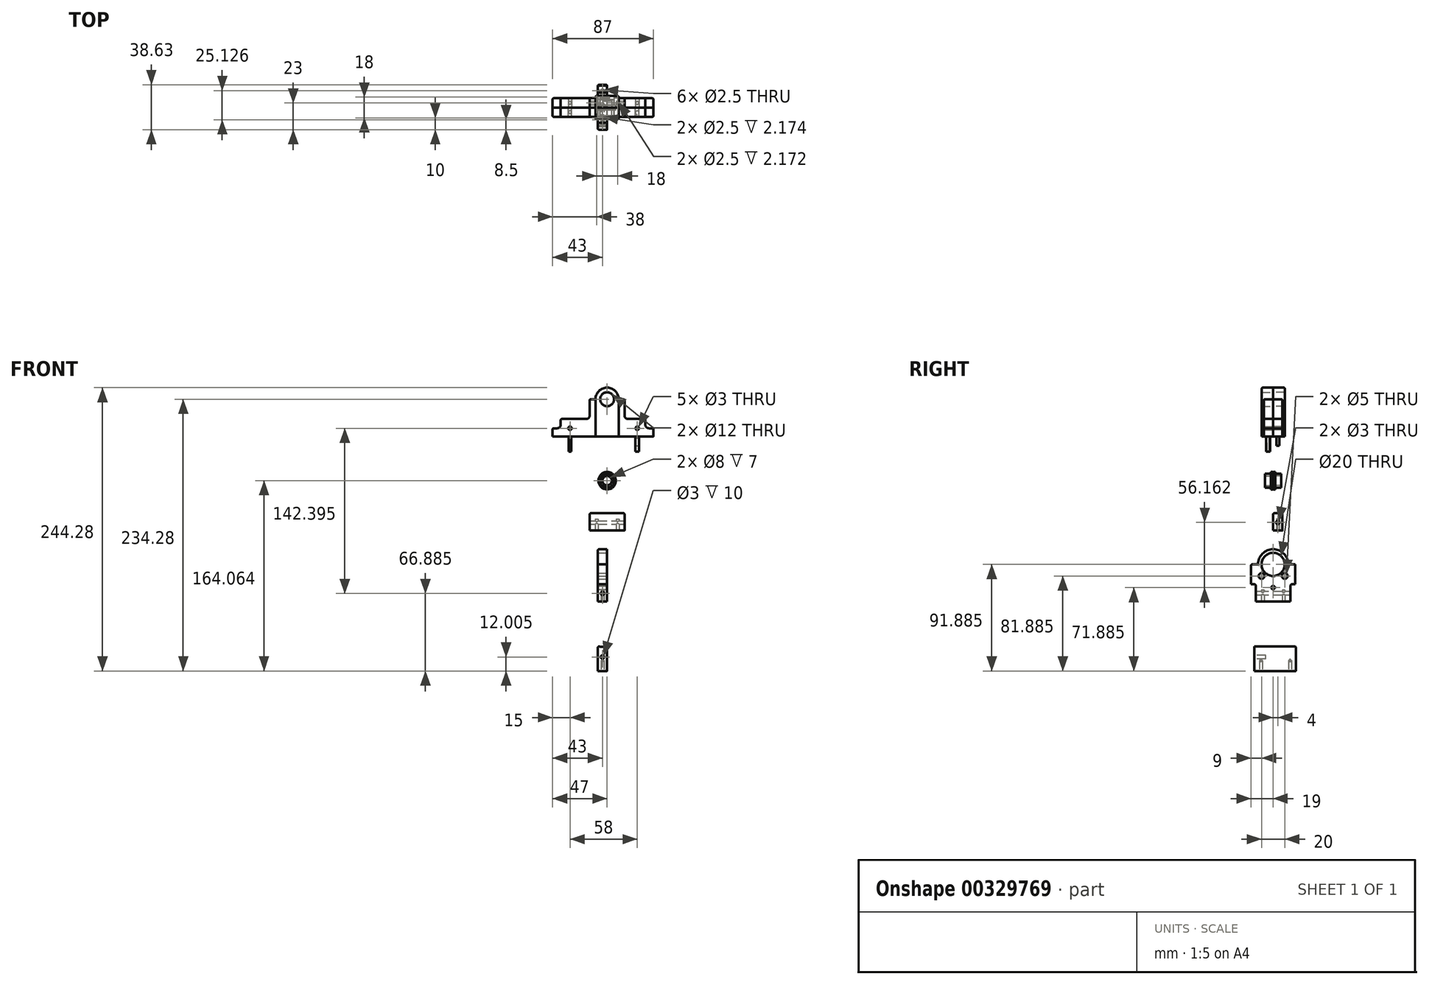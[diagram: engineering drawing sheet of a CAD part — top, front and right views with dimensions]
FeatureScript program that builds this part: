
annotation { "Feature Type Name" : "Feature", "Feature Type Description" : "" }
export const myFeature = defineFeature(function(context is Context, id is Id, definition is map)
    precondition{}
    {
        {
            var Q0;
            Q0=qCreatedBy(makeId("Front.planeOp"),FACE);
            var sketch = newSketch(context, id + "F0", { "sketchPlane" : qUnion([Q0])});
            skCircle(sketch, "E0", {"center": v(0, 32) * mm, "radius": 6 * mm});
            skArc(sketch, "E1", {"start": v(10, 32) * mm, "mid": v(0, 42) * mm, "end": v(-10, 32) * mm});
            skLineSegment(sketch, "E2", {"start": v(-47, 0) * mm, "end": v(40, 0) * mm});
            skLineSegment(sketch, "E3", {"start": v(40, 0) * mm, "end": v(40, 6) * mm});
            skLineSegment(sketch, "E4", {"start": v(39, 7) * mm, "end": v(36, 7) * mm});
            skLineSegment(sketch, "E5", {"start": v(33, 10) * mm, "end": v(33, 14) * mm});
            skLineSegment(sketch, "E6", {"start": v(32, 15) * mm, "end": v(18, 15) * mm});
            skLineSegment(sketch, "E7", {"start": v(15, 18) * mm, "end": v(15, 31) * mm});
            skLineSegment(sketch, "E8", {"start": v(14, 32) * mm, "end": v(10, 32) * mm});
            skPoint(sketch, "E9.visualSharp", {"position": v(40, 7) * mm});
            skArc(sketch, "E9.filletArc", {"start": v(40, 6) * mm, "mid": v(39.7, 6.7) * mm, "end": v(39, 7) * mm});
            skPoint(sketch, "E10.visualSharp", {"position": v(33, 15) * mm});
            skArc(sketch, "E10.filletArc", {"start": v(33, 14) * mm, "mid": v(32.7, 14.7) * mm, "end": v(32, 15) * mm});
            skPoint(sketch, "E11.visualSharp", {"position": v(15, 32) * mm});
            skArc(sketch, "E11.filletArc", {"start": v(15, 31) * mm, "mid": v(14.7, 31.7) * mm, "end": v(14, 32) * mm});
            skPoint(sketch, "E12.visualSharp", {"position": v(15, 15) * mm});
            skArc(sketch, "E12.filletArc", {"start": v(15, 18) * mm, "mid": v(15.88, 15.88) * mm, "end": v(18, 15) * mm});
            skPoint(sketch, "E13.visualSharp", {"position": v(33, 7) * mm});
            skArc(sketch, "E13.filletArc", {"start": v(33, 10) * mm, "mid": v(33.88, 7.88) * mm, "end": v(36, 7) * mm});
            skLineSegment(sketch, "E14", {"start": v(-47, 0) * mm, "end": v(-47, 6) * mm});
            skLineSegment(sketch, "E15", {"start": v(-46, 7) * mm, "end": v(-43, 7) * mm});
            skLineSegment(sketch, "E16", {"start": v(-40, 10) * mm, "end": v(-40, 14) * mm});
            skLineSegment(sketch, "E17", {"start": v(-39, 15) * mm, "end": v(-18, 15) * mm});
            skLineSegment(sketch, "E18", {"start": v(-15, 18) * mm, "end": v(-15, 31) * mm});
            skLineSegment(sketch, "E19", {"start": v(-14, 32) * mm, "end": v(-10, 32) * mm});
            skPoint(sketch, "E20.visualSharp", {"position": v(-15, 15) * mm});
            skArc(sketch, "E20.filletArc", {"start": v(-18, 15) * mm, "mid": v(-15.88, 15.88) * mm, "end": v(-15, 18) * mm});
            skPoint(sketch, "E21.visualSharp", {"position": v(-40, 7) * mm});
            skArc(sketch, "E21.filletArc", {"start": v(-43, 7) * mm, "mid": v(-40.88, 7.88) * mm, "end": v(-40, 10) * mm});
            skPoint(sketch, "E22.visualSharp", {"position": v(-15, 32) * mm});
            skArc(sketch, "E22.filletArc", {"start": v(-14, 32) * mm, "mid": v(-14.7, 31.7) * mm, "end": v(-15, 31) * mm});
            skPoint(sketch, "E23.visualSharp", {"position": v(-40, 15) * mm});
            skArc(sketch, "E23.filletArc", {"start": v(-39, 15) * mm, "mid": v(-39.7, 14.7) * mm, "end": v(-40, 14) * mm});
            skPoint(sketch, "E24.visualSharp", {"position": v(-47, 7) * mm});
            skArc(sketch, "E24.filletArc", {"start": v(-46, 7) * mm, "mid": v(-46.7, 6.7) * mm, "end": v(-47, 6) * mm});
            skCircle(sketch, "E25", {"center": v(26, 7) * mm, "radius": 1.5 * mm});
            skPoint(sketch, "E25.centerSnap0", {"position": v(37.5, 7) * mm});
            skCircle(sketch, "E26", {"center": v(-32, 7) * mm, "radius": 1.5 * mm});
            skPoint(sketch, "E26.centerSnap0", {"position": v(-44.5, 7) * mm});
            skSolve(sketch);
        }
        {
            var Q0;
            Q0 = qSketchRegion(id + "F0", true);
            extrude(context, id + "F1", {"entities" : qUnion([Q0]), "depth" : 8 * mm});
        }
        {
            var Q0;
            Q0=makeQuery(id+"F1.opExtrude","CAP_FACE",FACE,{"disambiguationData":[OSD([sQuery(id+"F0.wireOp",EDGE,"E0"),sQuery(id+"F0.wireOp",EDGE,"E1"),sQuery(id+"F0.wireOp",EDGE,"E2"),sQuery(id+"F0.wireOp",EDGE,"E3"),sQuery(id+"F0.wireOp",EDGE,"E4"),sQuery(id+"F0.wireOp",EDGE,"E5"),sQuery(id+"F0.wireOp",EDGE,"E6"),sQuery(id+"F0.wireOp",EDGE,"E7"),sQuery(id+"F0.wireOp",EDGE,"E8"),sQuery(id+"F0.wireOp",EDGE,"E9.filletArc"),sQuery(id+"F0.wireOp",EDGE,"E10.filletArc"),sQuery(id+"F0.wireOp",EDGE,"E11.filletArc"),sQuery(id+"F0.wireOp",EDGE,"E12.filletArc"),sQuery(id+"F0.wireOp",EDGE,"E13.filletArc"),sQuery(id+"F0.wireOp",EDGE,"E14"),sQuery(id+"F0.wireOp",EDGE,"E15"),sQuery(id+"F0.wireOp",EDGE,"E16"),sQuery(id+"F0.wireOp",EDGE,"E17"),sQuery(id+"F0.wireOp",EDGE,"E18"),sQuery(id+"F0.wireOp",EDGE,"E19"),sQuery(id+"F0.wireOp",EDGE,"E20.filletArc"),sQuery(id+"F0.wireOp",EDGE,"E21.filletArc"),sQuery(id+"F0.wireOp",EDGE,"E22.filletArc"),sQuery(id+"F0.wireOp",EDGE,"E23.filletArc"),sQuery(id+"F0.wireOp",EDGE,"E24.filletArc"),sQuery(id+"F0.wireOp",EDGE,"E25"),sQuery(id+"F0.wireOp",EDGE,"E26")])],"isStart":false});
            var sketch = newSketch(context, id + "F2", { "sketchPlane" : qUnion([Q0])});
            skCircle(sketch, "E27", {"center": v(0, 32) * mm, "radius": 6 * mm});
            skArc(sketch, "E28", {"start": v(10, 32) * mm, "mid": v(0, 42) * mm, "end": v(-10, 32) * mm});
            skLineSegment(sketch, "E29", {"start": v(-10, 32) * mm, "end": v(-10, 0) * mm});
            skLineSegment(sketch, "E30", {"start": v(10, 32) * mm, "end": v(10, 0) * mm});
            skLineSegment(sketch, "E31", {"start": v(10, 0) * mm, "end": v(-10, 0) * mm});
            skSolve(sketch);
        }
        {
            var Q0;
            Q0 = qSketchRegion(id + "F2", true);
            extrude(context, id + "F3", {"entities" : qUnion([Q0]), "operationType" : NewBodyOperationType.ADD, "depth" : 2 * mm});
        }
        {
            var Q0;
            Q0=makeQuery(id+"F1.opExtrude","CAP_EDGE",EDGE,{"disambiguationData":[OSD([sQuery(id+"F0.wireOp",EDGE,"E6")])],"isStart":false});
            var Q1;
            Q1=makeQuery(id+"F1.opExtrude","CAP_EDGE",EDGE,{"disambiguationData":[OSD([sQuery(id+"F0.wireOp",EDGE,"E17")])],"isStart":false});
            var Q2;
            Q2=makeQuery(id+"F3.opExtrude","CAP_EDGE",EDGE,{"disambiguationData":[OSD([sQuery(id+"F2.wireOp",EDGE,"E28")])],"isStart":false});
            fillet(context, id + "F4", {"entities" : qUnion([Q0, Q1, Q2]), "radius" : 1 * mm, "tangentPropagation" : true, "allowEdgeOverflow" : false});
        }
        {
            var Q0;
            Q0=makeQuery(id+"F1.opExtrude","SWEPT_BODY",BODY,{"disambiguationData":[OSD([sQuery(id+"F0.wireOp",EDGE,"E0"),sQuery(id+"F0.wireOp",EDGE,"E1"),sQuery(id+"F0.wireOp",EDGE,"E2"),sQuery(id+"F0.wireOp",EDGE,"E3"),sQuery(id+"F0.wireOp",EDGE,"E4"),sQuery(id+"F0.wireOp",EDGE,"E5"),sQuery(id+"F0.wireOp",EDGE,"E6"),sQuery(id+"F0.wireOp",EDGE,"E7"),sQuery(id+"F0.wireOp",EDGE,"E8"),sQuery(id+"F0.wireOp",EDGE,"E9.filletArc"),sQuery(id+"F0.wireOp",EDGE,"E10.filletArc"),sQuery(id+"F0.wireOp",EDGE,"E11.filletArc"),sQuery(id+"F0.wireOp",EDGE,"E12.filletArc"),sQuery(id+"F0.wireOp",EDGE,"E13.filletArc"),sQuery(id+"F0.wireOp",EDGE,"E14"),sQuery(id+"F0.wireOp",EDGE,"E15"),sQuery(id+"F0.wireOp",EDGE,"E16"),sQuery(id+"F0.wireOp",EDGE,"E17"),sQuery(id+"F0.wireOp",EDGE,"E18"),sQuery(id+"F0.wireOp",EDGE,"E19"),sQuery(id+"F0.wireOp",EDGE,"E20.filletArc"),sQuery(id+"F0.wireOp",EDGE,"E21.filletArc"),sQuery(id+"F0.wireOp",EDGE,"E22.filletArc"),sQuery(id+"F0.wireOp",EDGE,"E23.filletArc"),sQuery(id+"F0.wireOp",EDGE,"E24.filletArc"),sQuery(id+"F0.wireOp",EDGE,"E25"),sQuery(id+"F0.wireOp",EDGE,"E26")])]});
            var Q1;
            Q1=qCreatedBy(makeId("Front.planeOp"),FACE);
            mirror(context, id + "F5", {"entities" : qUnion([Q0]), "mirrorPlane" : qUnion([Q1])});
        }
        {
            var Q0;
            Q0=qCreatedBy(makeId("Front.planeOp"),FACE);
            var sketch = newSketch(context, id + "F6", { "sketchPlane" : qUnion([Q0])});
            skCircle(sketch, "E32", {"center": v(0, -38.22) * mm, "radius": 4 * mm});
            skCircle(sketch, "E33", {"center": v(0, -38.22) * mm, "radius": 7.5 * mm});
            skSolve(sketch);
        }
        {
            var Q0;
            Q0 = qSketchRegion(id + "F6", true);
            extrude(context, id + "F7", {"entities" : qUnion([Q0]), "oppositeDirection" : true, "depth" : 7 * mm});
        }
        {
            var Q0;
            Q0=makeQuery(id+"F7.opExtrude","CAP_FACE",FACE,{"disambiguationData":[OSD([sQuery(id+"F6.wireOp",EDGE,"E32"),sQuery(id+"F6.wireOp",EDGE,"E33")])],"isStart":false});
            var sketch = newSketch(context, id + "F8", { "sketchPlane" : qUnion([Q0])});
            skCircle(sketch, "E34", {"center": v(0, -38.22) * mm, "radius": 6 * mm});
            skCircle(sketch, "E35", {"center": v(0, -38.22) * mm, "radius": 7.5 * mm});
            skSolve(sketch);
        }
        {
            var Q0;
            Q0 = qSketchRegion(id + "F8", true);
            extrude(context, id + "F9", {"entities" : qUnion([Q0]), "operationType" : NewBodyOperationType.REMOVE, "oppositeDirection" : true, "depth" : 5 * mm});
        }
        {
            var Q0;
            Q0=makeQuery(id+"F7.opExtrude","CAP_EDGE",EDGE,{"disambiguationData":[OSD([sQuery(id+"F6.wireOp",EDGE,"E33")])],"isStart":true});
            fillet(context, id + "F10", {"entities" : qUnion([Q0]), "radius" : .5 * mm, "tangentPropagation" : true, "allowEdgeOverflow" : false});
        }
        {
            var Q0;
            Q0=makeQuery(id+"F7.opExtrude","SWEPT_BODY",BODY,{"disambiguationData":[OSD([sQuery(id+"F6.wireOp",EDGE,"E32"),sQuery(id+"F6.wireOp",EDGE,"E33")])]});
            var Q1;
            Q1=qCreatedBy(makeId("Front.planeOp"),FACE);
            mirror(context, id + "F11", {"entities" : qUnion([Q0]), "mirrorPlane" : qUnion([Q1])});
        }
        {
            var Q0;
            Q0=qCreatedBy(makeId("Front.planeOp"),FACE);
            var sketch = newSketch(context, id + "F12", { "sketchPlane" : qUnion([Q0])});
            skLineSegment(sketch, "E36.bottom", {"start": v(15, -66.23) * mm, "end": v(-15, -66.23) * mm});
            skLineSegment(sketch, "E36.top", {"start": v(15, -81.23) * mm, "end": v(-15, -81.23) * mm});
            skLineSegment(sketch, "E36.left", {"start": v(15, -66.23) * mm, "end": v(15, -81.23) * mm});
            skLineSegment(sketch, "E36.right", {"start": v(-15, -66.23) * mm, "end": v(-15, -81.23) * mm});
            skPoint(sketch, "E36.middle", {"position": v(0, -73.73) * mm});
            skSolve(sketch);
        }
        {
            var Q0;
            Q0 = qSketchRegion(id + "F12", true);
            extrude(context, id + "F13", {"entities" : qUnion([Q0]), "oppositeDirection" : true, "depth" : 8 * mm});
        }
        {
            var Q0;
            Q0=makeQuery(id+"F13.opExtrude","SWEPT_FACE",FACE,{"disambiguationData":[OSD([sQuery(id+"F12.wireOp",EDGE,"E36.left")])]});
            var sketch = newSketch(context, id + "F14", { "sketchPlane" : qUnion([Q0])});
            skCircle(sketch, "E37", {"center": v(4, -74.23) * mm, "radius": 1.5 * mm});
            skSolve(sketch);
        }
        {
            var Q0;
            Q0 = qSketchRegion(id + "F14", true);
            extrude(context, id + "F15", {"entities" : qUnion([Q0]), "operationType" : NewBodyOperationType.REMOVE, "oppositeDirection" : true, "depth" : 35 * mm});
        }
        {
            var Q0;
            Q0=makeQuery(id+"F13.opExtrude","SWEPT_FACE",FACE,{"disambiguationData":[OSD([sQuery(id+"F12.wireOp",EDGE,"E36.top")])]});
            var sketch = newSketch(context, id + "F16", { "sketchPlane" : qUnion([Q0])});
            skCircle(sketch, "E38", {"center": v(-9, -4) * mm, "radius": 1.25 * mm});
            skCircle(sketch, "E39", {"center": v(9, -4) * mm, "radius": 1.25 * mm});
            skSolve(sketch);
        }
        {
            var Q0;
            Q0 = qSketchRegion(id + "F16", true);
            extrude(context, id + "F17", {"entities" : qUnion([Q0]), "operationType" : NewBodyOperationType.REMOVE, "oppositeDirection" : true, "depth" : 10 * mm});
        }
        {
            var Q0;
            Q0=makeQuery(id+"F13.opExtrude","SWEPT_EDGE",EDGE,{"disambiguationData":[OSD([sQuery(id+"F12.wireOp",EDGE,"E36.bottom"),sQuery(id+"F12.wireOp",EDGE,"E36.left")])]});
            var Q1;
            Q1=makeQuery(id+"F13.opExtrude","CAP_EDGE",EDGE,{"disambiguationData":[OSD([sQuery(id+"F12.wireOp",EDGE,"E36.left")])],"isStart":true});
            var Q2;
            Q2=makeQuery(id+"F13.opExtrude","CAP_EDGE",EDGE,{"disambiguationData":[OSD([sQuery(id+"F12.wireOp",EDGE,"E36.bottom")])],"isStart":true});
            var Q3;
            Q3=makeQuery(id+"F13.opExtrude","CAP_EDGE",EDGE,{"disambiguationData":[OSD([sQuery(id+"F12.wireOp",EDGE,"E36.right")])],"isStart":true});
            var Q4;
            Q4=makeQuery(id+"F13.opExtrude","SWEPT_EDGE",EDGE,{"disambiguationData":[OSD([sQuery(id+"F12.wireOp",EDGE,"E36.bottom"),sQuery(id+"F12.wireOp",EDGE,"E36.right")])]});
            var Q5;
            Q5=makeQuery(id+"F13.opExtrude","CAP_EDGE",EDGE,{"disambiguationData":[OSD([sQuery(id+"F12.wireOp",EDGE,"E36.right")])],"isStart":false});
            var Q6;
            Q6=makeQuery(id+"F13.opExtrude","CAP_EDGE",EDGE,{"disambiguationData":[OSD([sQuery(id+"F12.wireOp",EDGE,"E36.left")])],"isStart":false});
            fillet(context, id + "F18", {"entities" : qUnion([Q0, Q1, Q2, Q3, Q4, Q5, Q6]), "radius" : 1 * mm, "tangentPropagation" : true, "allowEdgeOverflow" : false});
        }
        {
            var Q0;
            Q0=qCreatedBy(makeId("Right.planeOp"),FACE);
            var sketch = newSketch(context, id + "F19", { "sketchPlane" : qUnion([Q0])});
            skLineSegment(sketch, "E40", {"start": v(0, 0) * mm, "end": v(0, -162.85) * mm, "construction": true});
            skLineSegment(sketch, "E41", {"start": v(13, -110.4) * mm, "end": v(19, -110.4) * mm});
            skLineSegment(sketch, "E42", {"start": v(19, -110.4) * mm, "end": v(19, -127.4) * mm});
            skLineSegment(sketch, "E43", {"start": v(19, -127.4) * mm, "end": v(16.5, -127.4) * mm});
            skLineSegment(sketch, "E44", {"start": v(15, -128.9) * mm, "end": v(15, -142.4) * mm});
            skLineSegment(sketch, "E45", {"start": v(15, -142.4) * mm, "end": v(-15, -142.4) * mm});
            skLineSegment(sketch, "E46", {"start": v(-15, -142.4) * mm, "end": v(-15, -128.9) * mm});
            skLineSegment(sketch, "E47", {"start": v(-16.5, -127.4) * mm, "end": v(-19, -127.4) * mm});
            skLineSegment(sketch, "E48", {"start": v(-19, -127.4) * mm, "end": v(-19, -110.4) * mm});
            skLineSegment(sketch, "E49", {"start": v(-19, -110.4) * mm, "end": v(-13, -110.4) * mm});
            skCircle(sketch, "E50", {"center": v(0, -110.4) * mm, "radius": 10 * mm});
            skArc(sketch, "E51", {"start": v(13, -110.4) * mm, "mid": v(0, -97.4) * mm, "end": v(-13, -110.4) * mm});
            skCircle(sketch, "E52", {"center": v(10, -120.4) * mm, "radius": 2.5 * mm});
            skCircle(sketch, "E53", {"center": v(-10, -120.4) * mm, "radius": 2.5 * mm});
            skCircle(sketch, "E54", {"center": v(0, -130.4) * mm, "radius": 1.5 * mm});
            skPoint(sketch, "E55.visualSharp", {"position": v(15, -127.4) * mm});
            skArc(sketch, "E55.filletArc", {"start": v(16.5, -127.4) * mm, "mid": v(15.44, -127.83) * mm, "end": v(15, -128.9) * mm});
            skPoint(sketch, "E56.visualSharp", {"position": v(-15, -127.4) * mm});
            skArc(sketch, "E56.filletArc", {"start": v(-15, -128.9) * mm, "mid": v(-15.44, -127.83) * mm, "end": v(-16.5, -127.4) * mm});
            skSolve(sketch);
        }
        {
            var Q0;
            Q0 = qSketchRegion(id + "F19", true);
            extrude(context, id + "F20", {"entities" : qUnion([Q0]), "oppositeDirection" : true, "depth" : 8 * mm});
        }
        {
            var Q0;
            Q0=makeQuery(id+"F20.opExtrude","SWEPT_FACE",FACE,{"disambiguationData":[OSD([sQuery(id+"F19.wireOp",EDGE,"E46")])]});
            var sketch = newSketch(context, id + "F21", { "sketchPlane" : qUnion([Q0])});
            skCircle(sketch, "E57", {"center": v(-4, -135.4) * mm, "radius": 1.5 * mm});
            skSolve(sketch);
        }
        {
            var Q0;
            Q0 = qSketchRegion(id + "F21", true);
            extrude(context, id + "F22", {"entities" : qUnion([Q0]), "operationType" : NewBodyOperationType.REMOVE, "oppositeDirection" : true, "depth" : 35 * mm});
        }
        {
            var Q0;
            Q0=makeQuery(id+"F20.opExtrude","SWEPT_FACE",FACE,{"disambiguationData":[OSD([sQuery(id+"F19.wireOp",EDGE,"E45")])]});
            var sketch = newSketch(context, id + "F23", { "sketchPlane" : qUnion([Q0])});
            skCircle(sketch, "E58", {"center": v(-4, 9) * mm, "radius": 1.25 * mm});
            skCircle(sketch, "E59", {"center": v(-4, -9) * mm, "radius": 1.25 * mm});
            skSolve(sketch);
        }
        {
            var Q0;
            Q0 = qSketchRegion(id + "F23", true);
            extrude(context, id + "F24", {"entities" : qUnion([Q0]), "operationType" : NewBodyOperationType.REMOVE, "oppositeDirection" : true, "depth" : 10 * mm});
        }
        {
            var Q0;
            Q0=makeQuery(id+"F20.opExtrude","CAP_EDGE",EDGE,{"disambiguationData":[OSD([sQuery(id+"F19.wireOp",EDGE,"E51")])],"isStart":false});
            var Q1;
            Q1=makeQuery(id+"F20.opExtrude","SWEPT_EDGE",EDGE,{"disambiguationData":[OSD([sQuery(id+"F19.wireOp",EDGE,"E48"),sQuery(id+"F19.wireOp",EDGE,"E49")])]});
            var Q2;
            Q2=makeQuery(id+"F20.opExtrude","CAP_EDGE",EDGE,{"disambiguationData":[OSD([sQuery(id+"F19.wireOp",EDGE,"E49")])],"isStart":false});
            var Q3;
            Q3=makeQuery(id+"F20.opExtrude","CAP_EDGE",EDGE,{"disambiguationData":[OSD([sQuery(id+"F19.wireOp",EDGE,"E41")])],"isStart":false});
            var Q4;
            Q4=makeQuery(id+"F20.opExtrude","CAP_EDGE",EDGE,{"disambiguationData":[OSD([sQuery(id+"F19.wireOp",EDGE,"E48")])],"isStart":false});
            var Q5;
            Q5=makeQuery(id+"F20.opExtrude","CAP_EDGE",EDGE,{"disambiguationData":[OSD([sQuery(id+"F19.wireOp",EDGE,"E42")])],"isStart":false});
            fillet(context, id + "F25", {"entities" : qUnion([Q0, Q1, Q2, Q3, Q4, Q5]), "radius" : 1 * mm, "tangentPropagation" : true, "allowEdgeOverflow" : false});
        }
        {
            var Q0;
            Q0=qCreatedBy(makeId("Right.planeOp"),FACE);
            var sketch = newSketch(context, id + "F26", { "sketchPlane" : qUnion([Q0])});
            skLineSegment(sketch, "E60.bottom", {"start": v(19.63, -202.28) * mm, "end": v(-16.37, -202.28) * mm});
            skLineSegment(sketch, "E60.top", {"start": v(19.63, -180.78) * mm, "end": v(-16.37, -180.78) * mm});
            skLineSegment(sketch, "E60.left", {"start": v(19.63, -202.28) * mm, "end": v(19.63, -180.78) * mm});
            skLineSegment(sketch, "E60.right", {"start": v(-16.37, -202.28) * mm, "end": v(-16.37, -180.78) * mm});
            skSolve(sketch);
        }
        {
            var Q0;
            Q0 = qSketchRegion(id + "F26", true);
            extrude(context, id + "F27", {"entities" : qUnion([Q0]), "oppositeDirection" : true, "depth" : 8 * mm});
        }
        {
            var Q0;
            Q0=makeQuery(id+"F27.opExtrude","SWEPT_FACE",FACE,{"disambiguationData":[OSD([sQuery(id+"F26.wireOp",EDGE,"E60.right")])]});
            var sketch = newSketch(context, id + "F28", { "sketchPlane" : qUnion([Q0])});
            skArc(sketch, "E61", {"start": v(-8, -180.78) * mm, "mid": v(-4, -181.53) * mm, "end": v(0, -180.78) * mm});
            skLineSegment(sketch, "E62", {"start": v(-8, -180.78) * mm, "end": v(0, -180.78) * mm});
            skSolve(sketch);
        }
        {
            var Q0;
            Q0 = qSketchRegion(id + "F28", true);
            extrude(context, id + "F29", {"entities" : qUnion([Q0]), "operationType" : NewBodyOperationType.REMOVE, "oppositeDirection" : true, "depth" : 40 * mm});
        }
        {
            var Q0;
            Q0=makeQuery(id+"F27.opExtrude","SWEPT_FACE",FACE,{"disambiguationData":[OSD([sQuery(id+"F26.wireOp",EDGE,"E60.right")])]});
            var sketch = newSketch(context, id + "F30", { "sketchPlane" : qUnion([Q0])});
            skCircle(sketch, "E63", {"center": v(-4, -190.28) * mm, "radius": 1.5 * mm});
            skSolve(sketch);
        }
        {
            var Q0;
            Q0 = qSketchRegion(id + "F30", true);
            extrude(context, id + "F31", {"entities" : qUnion([Q0]), "operationType" : NewBodyOperationType.REMOVE, "oppositeDirection" : true, "depth" : 10 * mm});
        }
        {
            var Q0;
            Q0=makeQuery(id+"F27.opExtrude","SWEPT_FACE",FACE,{"disambiguationData":[OSD([sQuery(id+"F26.wireOp",EDGE,"E60.bottom")])]});
            var sketch = newSketch(context, id + "F32", { "sketchPlane" : qUnion([Q0])});
            skCircle(sketch, "E64", {"center": v(-4, 10.5) * mm, "radius": 1.25 * mm});
            skCircle(sketch, "E65", {"center": v(-4, -14.63) * mm, "radius": 1.25 * mm});
            skSolve(sketch);
        }
        {
            var Q0;
            Q0 = qSketchRegion(id + "F32", true);
            extrude(context, id + "F33", {"entities" : qUnion([Q0]), "operationType" : NewBodyOperationType.REMOVE, "oppositeDirection" : true, "depth" : 10 * mm});
        }
        {
            var Q0;
            Q0=makeQuery(id+"F29.boolean.opBoolean","COPY",EDGE,{"derivedFrom":makeQuery(id+"F29.opExtrude","CAP_EDGE",EDGE,{"disambiguationData":[OSD([sQuery(id+"F28.wireOp",EDGE,"E61")])],"isStart":true})});
            var Q1;
            {var subQ0=sQuery(id+"F28.wireOp",EDGE,"E62");var subQ1=sQuery(id+"F28.wireOp",EDGE,"E61");var subQ2=sQuery(id+"F26.wireOp",EDGE,"E60.right");Q1=makeQuery(id+"F29.boolean.opBoolean","MERGE",EDGE,{"derivedFrom":[makeQuery(id+"F27.opExtrude","CAP_EDGE",EDGE,{"disambiguationData":[OSD([sQuery(id+"F26.wireOp",EDGE,"E60.top")])],"isStart":false}),makeQuery(id+"F29.opExtrude","SWEPT_EDGE",EDGE,{"disambiguationData":[OSD([subQ2,subQ1,subQ0]),TDD([makeQuery(id+"F28.imprint","INTERSECT",VERTEX,{"derivedFrom":[makeQuery(id+"F27.opExtrude","CAP_EDGE",EDGE,{"disambiguationData":[OSD([subQ2])],"isStart":false}),subQ1,subQ0]})])]})]});}
            var Q2;
            Q2=makeQuery(id+"F27.opExtrude","CAP_EDGE",EDGE,{"disambiguationData":[OSD([sQuery(id+"F26.wireOp",EDGE,"E60.right")])],"isStart":false});
            var Q3;
            Q3=makeQuery(id+"F27.opExtrude","CAP_EDGE",EDGE,{"disambiguationData":[OSD([sQuery(id+"F26.wireOp",EDGE,"E60.right")])],"isStart":true});
            var Q4;
            Q4=makeQuery(id+"F33.boolean.opBoolean","COPY",EDGE,{"derivedFrom":makeQuery(id+"F33.opExtrude","CAP_EDGE",EDGE,{"disambiguationData":[OSD([sQuery(id+"F32.wireOp",EDGE,"E64")])],"isStart":false})});
            var Q5;
            Q5=makeQuery(id+"F33.boolean.opBoolean","COPY",EDGE,{"derivedFrom":makeQuery(id+"F33.opExtrude","CAP_EDGE",EDGE,{"disambiguationData":[OSD([sQuery(id+"F32.wireOp",EDGE,"E65")])],"isStart":false})});
            var Q6;
            Q6=makeQuery(id+"F27.opExtrude","CAP_EDGE",EDGE,{"disambiguationData":[OSD([sQuery(id+"F26.wireOp",EDGE,"E60.left")])],"isStart":false});
            var Q7;
            Q7=makeQuery(id+"F29.boolean.opBoolean","INTERSECT",EDGE,{"derivedFrom":[makeQuery(id+"F27.opExtrude","SWEPT_FACE",FACE,{"disambiguationData":[OSD([sQuery(id+"F26.wireOp",EDGE,"E60.left")])]}),makeQuery(id+"F29.opExtrude","SWEPT_FACE",FACE,{"disambiguationData":[OSD([sQuery(id+"F28.wireOp",EDGE,"E61")])]})]});
            var Q8;
            {var subQ0=sQuery(id+"F28.wireOp",EDGE,"E62");var subQ1=sQuery(id+"F28.wireOp",EDGE,"E61");var subQ2=sQuery(id+"F26.wireOp",EDGE,"E60.right");Q8=makeQuery(id+"F29.boolean.opBoolean","MERGE",EDGE,{"derivedFrom":[makeQuery(id+"F27.opExtrude","CAP_EDGE",EDGE,{"disambiguationData":[OSD([sQuery(id+"F26.wireOp",EDGE,"E60.top")])],"isStart":true}),makeQuery(id+"F29.opExtrude","SWEPT_EDGE",EDGE,{"disambiguationData":[OSD([subQ2,subQ1,subQ0]),TDD([makeQuery(id+"F28.imprint","INTERSECT",VERTEX,{"derivedFrom":[makeQuery(id+"F27.opExtrude","CAP_EDGE",EDGE,{"disambiguationData":[OSD([subQ2])],"isStart":true}),subQ1,subQ0]})])]})]});}
            var Q9;
            Q9=makeQuery(id+"F27.opExtrude","CAP_EDGE",EDGE,{"disambiguationData":[OSD([sQuery(id+"F26.wireOp",EDGE,"E60.left")])],"isStart":true});
            fillet(context, id + "F34", {"entities" : qUnion([Q0, Q1, Q2, Q3, Q4, Q5, Q6, Q7, Q8, Q9]), "radius" : 1 * mm, "tangentPropagation" : true, "allowEdgeOverflow" : false});
        }
        {
            var Q0;
            Q0=makeQuery(id+"F3.boolean.opBoolean","MERGE",FACE,{"derivedFrom":[makeQuery(id+"F1.opExtrude","SWEPT_FACE",FACE,{"disambiguationData":[OSD([sQuery(id+"F0.wireOp",EDGE,"E2")])]}),makeQuery(id+"F3.opExtrude","SWEPT_FACE",FACE,{"disambiguationData":[OSD([sQuery(id+"F2.wireOp",EDGE,"E31")])]})]});
            var sketch = newSketch(context, id + "F35", { "sketchPlane" : qUnion([Q0])});
            skCircle(sketch, "E66", {"center": v(26, 4.46) * mm, "radius": 1.59 * mm});
            skCircle(sketch, "E67", {"center": v(-32, 3.9) * mm, "radius": 1.25 * mm});
            skSolve(sketch);
        }
        {
            var Q0;
            Q0 = qSketchRegion(id + "F35", true);
            extrude(context, id + "F36", {"entities" : qUnion([Q0]), "operationType" : NewBodyOperationType.ADD, "depth" : 13 * mm});
        }
        {
            var Q0;
            Q0=makeQuery(id+"F5.opPattern","COPY",FACE,{"derivedFrom":makeQuery(id+"F3.boolean.opBoolean","MERGE",FACE,{"derivedFrom":[makeQuery(id+"F1.opExtrude","SWEPT_FACE",FACE,{"disambiguationData":[OSD([sQuery(id+"F0.wireOp",EDGE,"E2")])]}),makeQuery(id+"F3.opExtrude","SWEPT_FACE",FACE,{"disambiguationData":[OSD([sQuery(id+"F2.wireOp",EDGE,"E31")])]})]}),"instanceName":"1"});
            var sketch = newSketch(context, id + "F37", { "sketchPlane" : qUnion([Q0])});
            skCircle(sketch, "E68", {"center": v(26, -4) * mm, "radius": 1.25 * mm});
            skCircle(sketch, "E69", {"center": v(-32, -4.12) * mm, "radius": 1.25 * mm});
            skSolve(sketch);
        }
        {
            var Q0;
            Q0 = qSketchRegion(id + "F37", true);
            extrude(context, id + "F38", {"entities" : qUnion([Q0]), "operationType" : NewBodyOperationType.ADD, "depth" : 8 * mm});
        }
    });
